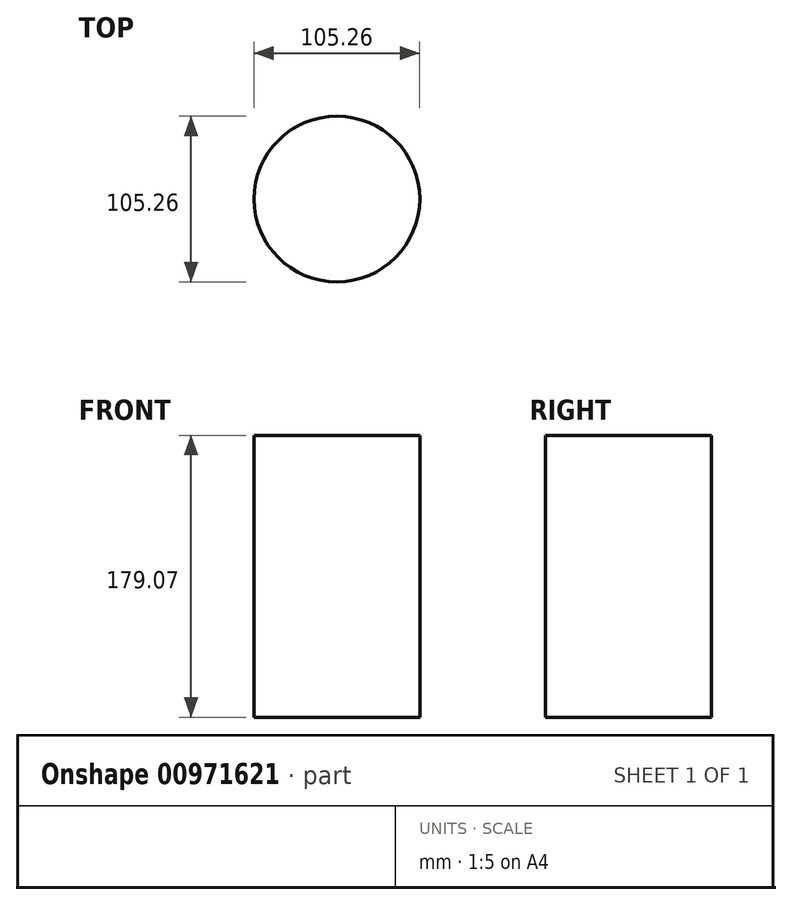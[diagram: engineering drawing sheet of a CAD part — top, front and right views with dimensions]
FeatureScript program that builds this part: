
annotation { "Feature Type Name" : "Feature", "Feature Type Description" : "" }
export const myFeature = defineFeature(function(context is Context, id is Id, definition is map)
    precondition{}
    {
        {
            var Q0;
            Q0=qCreatedBy(makeId("Front.planeOp"),FACE);
            var sketch = newSketch(context, id + "F0", { "sketchPlane" : qUnion([Q0])});
            skEllipse(sketch, "E0", {"center": v(-5.24, -5.77) * mm, "majorRadius": 95.9 * mm, "minorRadius": 99.9 * mm, "majorAxis": v(-0.85, -0.53)});
            skSolve(sketch);
        }
        {
            var Q0;
            Q0=sQuery(id+"F0.wireOp",EDGE,"E0");
            extrude(context, id + "F1", {"bodyType" : ToolBodyType.SURFACE, "surfaceEntities" : qUnion([Q0]), "depth" : 268.22 * mm, "offsetDistance" : 25.4 * mm});
        }
        {
            var Q0;
            Q0=qCreatedBy(makeId("Top.planeOp"),FACE);
            var sketch = newSketch(context, id + "F2", { "sketchPlane" : qUnion([Q0])});
            skCircle(sketch, "E1", {"center": v(0, 0) * mm, "radius": 52.63 * mm});
            skSolve(sketch);
        }
        {
            var Q0;
            Q0=makeQuery(id+"F2.imprint","IMPRINT",FACE,{"disambiguationData":[TD([[makeQuery(id+"F2.imprint","IMPRINT",EDGE,{"derivedFrom":sQuery(id+"F2.wireOp",EDGE,"E1")}),1.0]])]});
            extrude(context, id + "F3", {"entities" : qUnion([Q0]), "depth" : 179.07 * mm, "offsetDistance" : 25.4 * mm});
        }
    });
